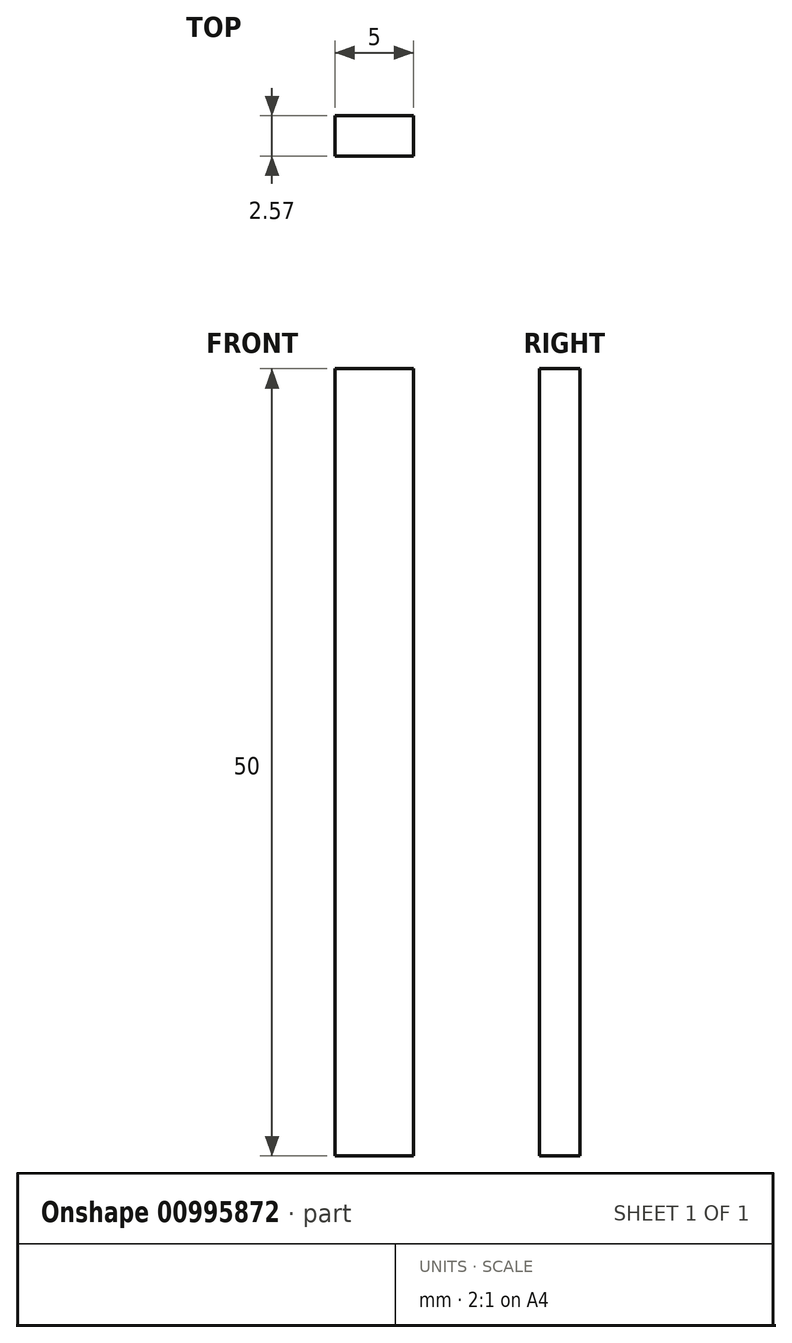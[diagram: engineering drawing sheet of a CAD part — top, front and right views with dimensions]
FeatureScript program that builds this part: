
annotation { "Feature Type Name" : "Feature", "Feature Type Description" : "" }
export const myFeature = defineFeature(function(context is Context, id is Id, definition is map)
    precondition{}
    {
        {
            var Q0;
            Q0=qCreatedBy(makeId("Top.planeOp"),FACE);
            var sketch = newSketch(context, id + "F0", { "sketchPlane" : qUnion([Q0])});
            skLineSegment(sketch, "E0.bottom", {"start": v(0, -0.22) * mm, "end": v(5, -0.22) * mm});
            skLineSegment(sketch, "E0.top", {"start": v(0, -2.8) * mm, "end": v(5, -2.8) * mm});
            skLineSegment(sketch, "E0.left", {"start": v(0, -0.22) * mm, "end": v(0, -2.8) * mm});
            skLineSegment(sketch, "E0.right", {"start": v(5, -0.22) * mm, "end": v(5, -2.8) * mm});
            skSolve(sketch);
        }
        {
            var Q0;
            Q0=makeQuery(id+"F0.imprint","IMPRINT",FACE,{"disambiguationData":[TD([[makeQuery(id+"F0.imprint","IMPRINT",EDGE,{"derivedFrom":sQuery(id+"F0.wireOp",EDGE,"E0.bottom")}),-1.0]])]});
            extrude(context, id + "F1", {"entities" : qUnion([Q0]), "depth" : 50 * mm, "offsetDistance" : 25 * mm});
        }
    });
